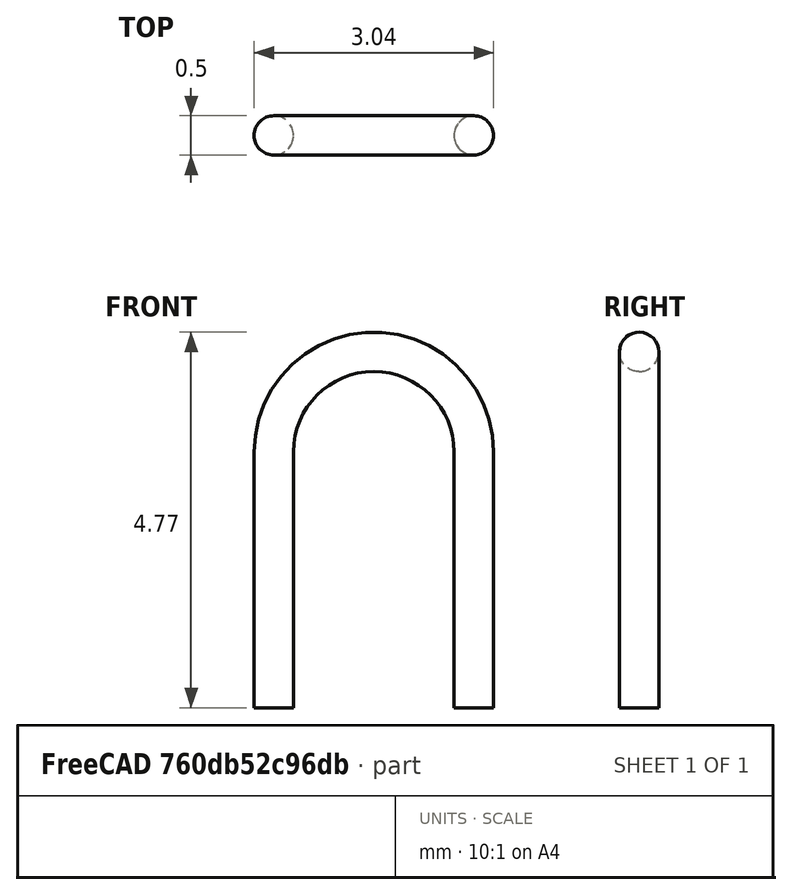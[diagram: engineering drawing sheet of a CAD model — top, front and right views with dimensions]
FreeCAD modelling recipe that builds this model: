
FCSTD DOCUMENT  (FreeCAD 0.17R12018 (Git))
Label: Test_Point_Bridge_Pitch2.54mm_Drill0.7mm
License: All rights reserved
LicenseURL: http://en.wikipedia.org/wiki/All_rights_reserved
objects: Sketcher::SketchObject×2, Spreadsheet::Sheet×1, PartDesign::SubtractivePipe×1, PartDesign::Body×1
note: 5 computed .brp shape members not serialized (recipe doc carries the construction recipe); baked Part::Feature solids carry a one-line shape summary decoded from their .brp

FEATURE [Sketcher::SketchObject] Sketch
  MapMode = 5
  Placement = pos=(0,0,-3) rot=(0,0,1;0rad)
  Support = -> [XY_Plane]
  superPlacement = pos=(0,0,-3) rot=(0,0,1;0rad)
  expr: Constraints[1] = dims.DWire / 2
  sketch-geometry (1):
    g0: Circle CenterX=0 CenterY=0 CenterZ=0 NormalX=0 NormalY=0 NormalZ=1 Radius=0.25
  constraints (2):
    c: Coincident(g0,g-1)
    c: Radius(g0) = 0.25
FEATURE [Spreadsheet::Sheet] Spreadsheet  label="dims"
  cells = A1="DWire"; B1(DWire)=0.5; A2="Pitch"; B2(Pitch)=2.54
FEATURE [Sketcher::SketchObject] Sketch001
  MapMode = 5
  Placement = pos=(0,0,0) rot=(1,0,0;1.5708rad)
  Support = -> [XZ_Plane]
  expr: Constraints[10] = dims.DWire / 2
  expr: Constraints[3] = dims.Pitch
  sketch-geometry (4):
    g0: LineSegment StartX=0 StartY=-3 StartZ=0 EndX=0 EndY=0.25 EndZ=0
    g1: LineSegment StartX=2.54 StartY=0.25 StartZ=0 EndX=2.54 EndY=-3 EndZ=0
    g2: LineSegment [constr] StartX=0 StartY=0.25 StartZ=0 EndX=2.54 EndY=0.25 EndZ=0
    g3: ArcOfCircle CenterX=1.27 CenterY=0.25 CenterZ=0 NormalX=0 NormalY=0 NormalZ=1 Radius=1.27 StartAngle=0 EndAngle=3.14159
  constraints (13):
    c: PointOnObject(g0,g-2)
    c: Vertical(g0)
    c: Vertical(g1)
    c: DistanceX(g0,g1) = 2.54
    c: Coincident(g2,g0)
    c: Coincident(g2,g1)
    c: Horizontal(g2)
    c: PointOnObject(g3,g2)
    c: Coincident(g3,g0)
    c: Coincident(g3,g1)
    c: DistanceY(g-1,g3) = 0.25
    c: DistanceY(g0,g-1) = 3
    c: Equal(g1,g0)
FEATURE [PartDesign::SubtractivePipe] SubtractivePipe
  AuxilleryCurvelinear = true
  AuxillerySpineTangent = false
  Binormal = (0,0,0)
  Mode = 0
  Profile = -> Sketch
  Spine = -> Sketch001
  SpineTangent = false
  Transformation = 0
  Transition = 0
FEATURE [PartDesign::Body] Body  label="Test_Point_Bridge_Pitch2.54mm_Drill0.7mm"
  Group = -> [Sketch,Sketch001,SubtractivePipe]
  Origin = -> Origin
  Tip = -> SubtractivePipe
